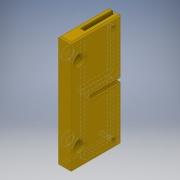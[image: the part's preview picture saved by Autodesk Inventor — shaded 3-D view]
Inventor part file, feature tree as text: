
AUTODESK INVENTOR PART (.ipt)
format: ipt  version: 2019 (Build 230136000, 136)  size: 182,784 bytes
history: native  units: mm
features: sketch x5, extrude x4, chamfer x2, hole x1
ambient origin geometry x8: Origin, YZ Plane, XZ Plane, XY Plane, X Axis, Y Axis, Z Axis, Center Point
bodies: Solid1 (feature_tree)
feature tree (12):
  extrude  "Extrusion1"  Depth=89.0mm
  extrude  "Extrusion2"  Depth=3.3mm
  extrude  "Extrusion3"  Depth=25.0mm
  hole  "Hole1"  [1 undecoded]
  chamfer  "Chamfer1"  Distance=19.5mm
  extrude  "Extrusion4"  Depth=1.0mm TaperAngle=45.0deg
  chamfer  "Chamfer2"  Distance=6.0mm
  sketch  "Sketch1"  dims[d0=10.0mm d1=89.0mm]
  sketch  "Sketch2"  dims[d2=40.0mm d3=0.0mm d4=3.3mm]
  sketch  "Sketch3"  dims[d5=26.0mm d6=0.0mm]
  sketch  "Sketch4"  dims[d8=3.0mm d9=6.0mm d10=4.0mm d11=2.0mm d12=90.0deg d13=26.75mm d14=0.0mm d15=25.0mm]
  sketch  "Sketch5"  dims[d16=3.2mm d17=16.0mm d18=0.0mm d19=19.5mm d20=1.0mm d21=2.0mm d22=45.0deg d23=6.0mm d24=33.0mm d25=15.0mm d26=15.0mm d27=10.0mm d28=0.0mm d29=2.0mm d30=2.0mm d31=45.0deg]
note: 1 required parameter value undecoded (feature->parameter linkage not recoverable at this tier; creation-order binding heuristic only, values carry confidence <= 0.55)
